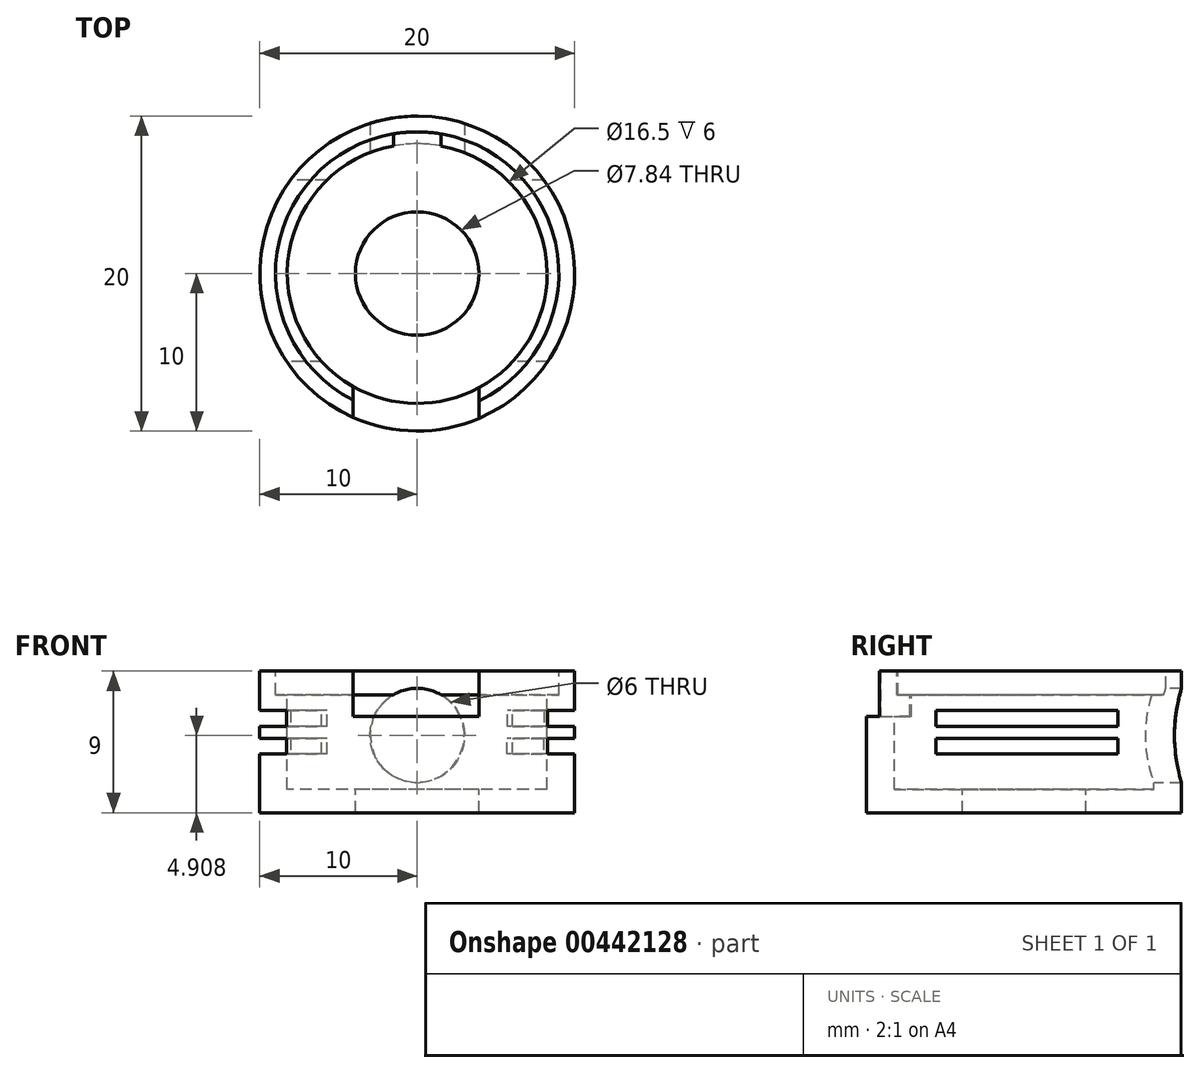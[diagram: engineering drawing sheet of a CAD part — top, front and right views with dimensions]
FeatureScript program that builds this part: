
annotation { "Feature Type Name" : "Feature", "Feature Type Description" : "" }
export const myFeature = defineFeature(function(context is Context, id is Id, definition is map)
    precondition{}
    {
        {
            var Q0;
            Q0=qCreatedBy(makeId("Top.planeOp"),FACE);
            var sketch = newSketch(context, id + "F0", { "sketchPlane" : qUnion([Q0])});
            skCircle(sketch, "E0", {"center": v(0, 0) * mm, "radius": 10 * mm});
            skSolve(sketch);
        }
        {
            var Q0;
            Q0 = qSketchRegion(id + "F0", true);
            extrude(context, id + "F1", {"entities" : qUnion([Q0]), "depth" : 9 * mm, "offsetDistance" : 25 * mm});
        }
        {
            var Q0;
            Q0=makeQuery(id+"F1.opExtrude","CAP_FACE",FACE,{"disambiguationData":[OSD([sQuery(id+"F0.wireOp",EDGE,"E0")])],"isStart":false});
            var sketch = newSketch(context, id + "F2", { "sketchPlane" : qUnion([Q0])});
            skCircle(sketch, "E1", {"center": v(0, 0) * mm, "radius": 9 * mm});
            skSolve(sketch);
        }
        {
            var Q0;
            Q0 = qSketchRegion(id + "F2", true);
            extrude(context, id + "F3", {"entities" : qUnion([Q0]), "operationType" : NewBodyOperationType.REMOVE, "oppositeDirection" : true, "depth" : 1.5 * mm, "offsetDistance" : 25 * mm});
        }
        {
            var Q0;
            Q0=makeQuery(id+"F3.boolean.opBoolean","COPY",FACE,{"derivedFrom":makeQuery(id+"F3.opExtrude","CAP_FACE",FACE,{"disambiguationData":[OSD([sQuery(id+"F2.wireOp",EDGE,"E1")])],"isStart":false})});
            var sketch = newSketch(context, id + "F4", { "sketchPlane" : qUnion([Q0])});
            skCircle(sketch, "E2", {"center": v(0, 0) * mm, "radius": 8.25 * mm});
            skSolve(sketch);
        }
        {
            var Q0;
            Q0=makeQuery(id+"F4.imprint","IMPRINT",FACE,{"disambiguationData":[TD([[makeQuery(id+"F4.imprint","IMPRINT",EDGE,{"derivedFrom":sQuery(id+"F4.wireOp",EDGE,"E2")}),1.0]])]});
            extrude(context, id + "F5", {"entities" : qUnion([Q0]), "operationType" : NewBodyOperationType.REMOVE, "oppositeDirection" : true, "depth" : 6 * mm, "offsetDistance" : 25 * mm});
        }
        {
            var Q0;
            Q0=makeQuery(id+"F5.boolean.opBoolean","COPY",FACE,{"derivedFrom":makeQuery(id+"F5.opExtrude","CAP_FACE",FACE,{"disambiguationData":[OSD([sQuery(id+"F4.wireOp",EDGE,"E2")])],"isStart":false})});
            var sketch = newSketch(context, id + "F6", { "sketchPlane" : qUnion([Q0])});
            skPoint(sketch, "E3", {"position": v(0, 8.25) * mm});
            skPoint(sketch, "E4", {"position": v(0, 0) * mm});
            skCircle(sketch, "E5", {"center": v(0, 0) * mm, "radius": 3.92 * mm});
            skSolve(sketch);
        }
        {
            var Q0;
            Q0 = qSketchRegion(id + "F6", true);
            extrude(context, id + "F7", {"entities" : qUnion([Q0]), "operationType" : NewBodyOperationType.REMOVE, "endBound" : BoundingType.THROUGH_ALL, "oppositeDirection" : true, "depth" : 25 * mm, "offsetDistance" : 25 * mm});
        }
        {
            var Q0;
            Q0=qCreatedBy(makeId("Front.planeOp"),FACE);
            var sketch = newSketch(context, id + "F8", { "sketchPlane" : qUnion([Q0])});
            skPoint(sketch, "E6", {"position": v(0, 0) * mm});
            skPoint(sketch, "E7", {"position": v(0, 4.9) * mm});
            skCircle(sketch, "E8", {"center": v(0, 4.9) * mm, "radius": 3 * mm});
            skSolve(sketch);
        }
        {
            var Q0;
            Q0 = qSketchRegion(id + "F8", true);
            extrude(context, id + "F9", {"entities" : qUnion([Q0]), "operationType" : NewBodyOperationType.REMOVE, "endBound" : BoundingType.THROUGH_ALL, "oppositeDirection" : true, "depth" : 25 * mm, "offsetDistance" : 25 * mm});
        }
        {
            var Q0;
            Q0=qCreatedBy(makeId("Front.planeOp"),FACE);
            var sketch = newSketch(context, id + "F10", { "sketchPlane" : qUnion([Q0])});
            skLineSegment(sketch, "E9.bottom", {"start": v(-4.08, 6.12) * mm, "end": v(3.94, 6.12) * mm});
            skLineSegment(sketch, "E9.top", {"start": v(-4.08, 9.01) * mm, "end": v(3.94, 9.01) * mm});
            skLineSegment(sketch, "E9.left", {"start": v(-4.08, 6.12) * mm, "end": v(-4.08, 9.01) * mm});
            skLineSegment(sketch, "E9.right", {"start": v(3.94, 6.12) * mm, "end": v(3.94, 9.01) * mm});
            skSolve(sketch);
        }
        {
            var Q0;
            Q0 = qSketchRegion(id + "F10", true);
            extrude(context, id + "F11", {"entities" : qUnion([Q0]), "operationType" : NewBodyOperationType.REMOVE, "depth" : 25 * mm, "offsetDistance" : 25 * mm});
        }
        {
            var Q0;
            Q0=qCreatedBy(makeId("Right.planeOp"),FACE);
            var sketch = newSketch(context, id + "F12", { "sketchPlane" : qUnion([Q0])});
            skLineSegment(sketch, "E10.bottom", {"start": v(-5.6, 6.49) * mm, "end": v(5.94, 6.49) * mm});
            skLineSegment(sketch, "E10.top", {"start": v(-5.6, 5.48) * mm, "end": v(5.94, 5.48) * mm});
            skLineSegment(sketch, "E10.left", {"start": v(-5.6, 6.49) * mm, "end": v(-5.6, 5.48) * mm});
            skLineSegment(sketch, "E10.right", {"start": v(5.94, 6.49) * mm, "end": v(5.94, 5.48) * mm});
            skLineSegment(sketch, "E11.bottom", {"start": v(-5.59, 4.74) * mm, "end": v(5.95, 4.74) * mm});
            skLineSegment(sketch, "E11.top", {"start": v(-5.59, 3.73) * mm, "end": v(5.95, 3.73) * mm});
            skLineSegment(sketch, "E11.left", {"start": v(-5.59, 4.74) * mm, "end": v(-5.59, 3.73) * mm});
            skLineSegment(sketch, "E11.right", {"start": v(5.95, 4.74) * mm, "end": v(5.95, 3.73) * mm});
            skSolve(sketch);
        }
        {
            var Q0;
            Q0 = qSketchRegion(id + "F12", true);
            extrude(context, id + "F13", {"entities" : qUnion([Q0]), "operationType" : NewBodyOperationType.REMOVE, "endBound" : BoundingType.SYMMETRIC, "depth" : 50 * mm, "offsetDistance" : 25 * mm});
        }
    });
